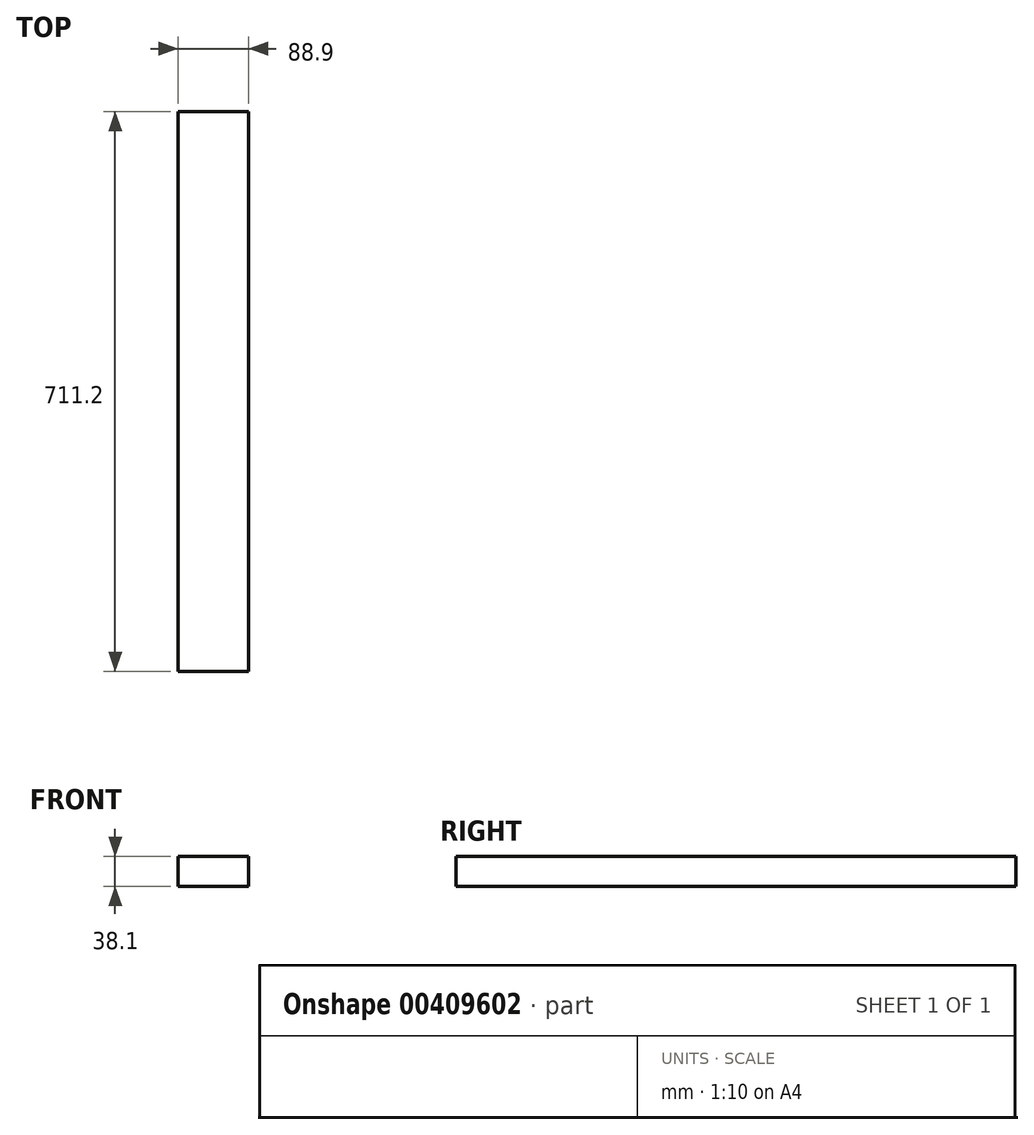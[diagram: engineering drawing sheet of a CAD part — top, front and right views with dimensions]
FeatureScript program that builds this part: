
annotation { "Feature Type Name" : "Feature", "Feature Type Description" : "" }
export const myFeature = defineFeature(function(context is Context, id is Id, definition is map)
    precondition{}
    {
        {
            var Q0;
            Q0=qCreatedBy(makeId("Front.planeOp"),FACE);
            var sketch = newSketch(context, id + "F0", { "sketchPlane" : qUnion([Q0])});
            skLineSegment(sketch, "E0.bottom", {"start": v(44.45, -19.05) * mm, "end": v(-44.45, -19.05) * mm});
            skLineSegment(sketch, "E0.top", {"start": v(44.45, 19.05) * mm, "end": v(-44.45, 19.05) * mm});
            skLineSegment(sketch, "E0.left", {"start": v(44.45, -19.05) * mm, "end": v(44.45, 19.05) * mm});
            skLineSegment(sketch, "E0.right", {"start": v(-44.45, -19.05) * mm, "end": v(-44.45, 19.05) * mm});
            skPoint(sketch, "E0.middle", {"position": v(0, 0) * mm});
            skSolve(sketch);
        }
        {
            var Q0;
            Q0=makeQuery(id+"F0.imprint","IMPRINT",FACE,{"disambiguationData":[TD([[makeQuery(id+"F0.imprint","IMPRINT",EDGE,{"derivedFrom":sQuery(id+"F0.wireOp",EDGE,"E0.bottom")}),-1.0]])]});
            extrude(context, id + "F1", {"entities" : qUnion([Q0]), "endBound" : BoundingType.SYMMETRIC, "depth" : 711.2 * mm});
        }
    });
